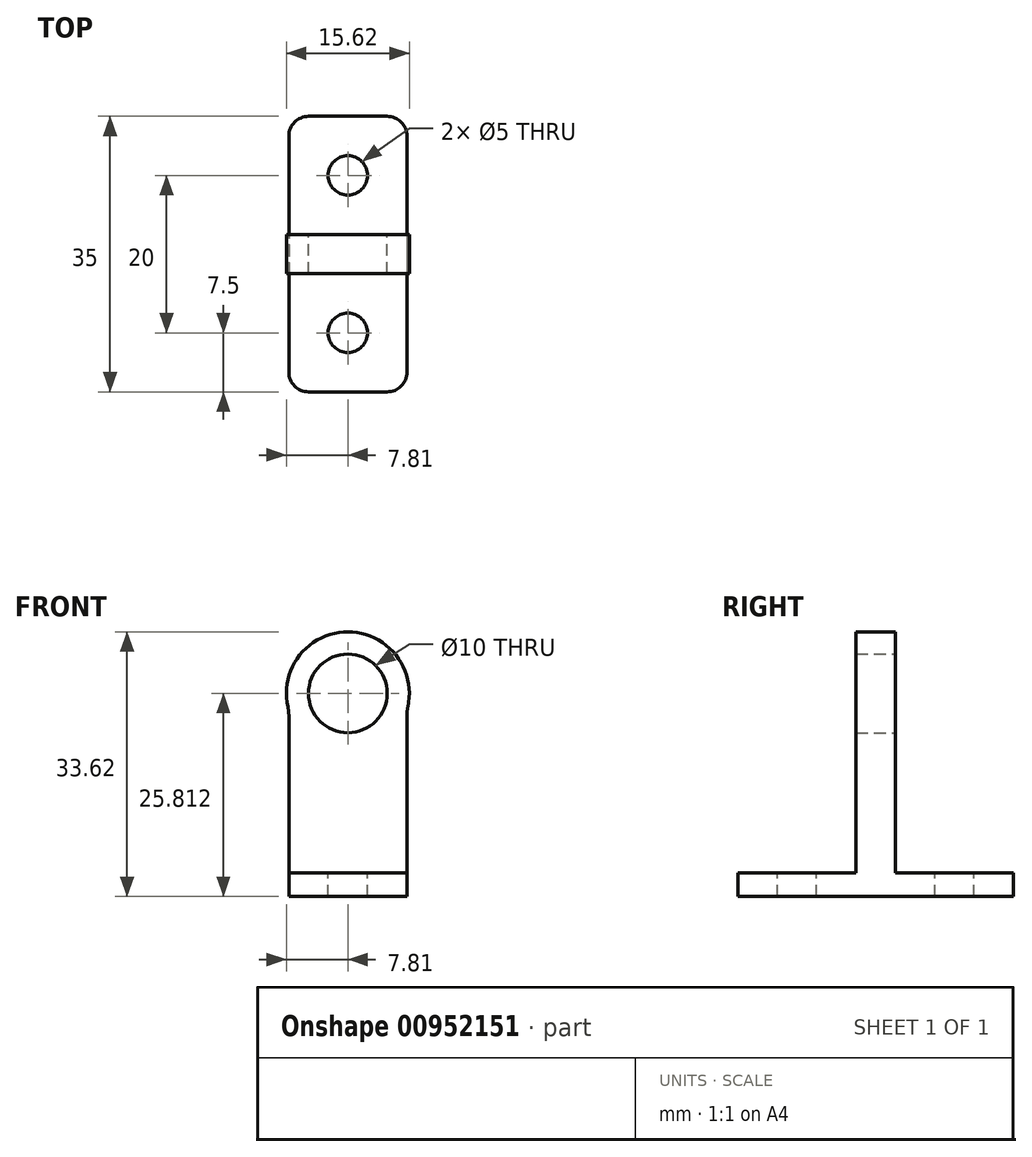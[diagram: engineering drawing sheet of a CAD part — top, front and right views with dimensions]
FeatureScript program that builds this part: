
annotation { "Feature Type Name" : "Feature", "Feature Type Description" : "" }
export const myFeature = defineFeature(function(context is Context, id is Id, definition is map)
    precondition{}
    {
        {
            var Q0;
            Q0=qCreatedBy(makeId("Top.planeOp"),FACE);
            var sketch = newSketch(context, id + "F0", { "sketchPlane" : qUnion([Q0])});
            skLineSegment(sketch, "E0.bottom", {"start": v(-7.5, 17.5) * mm, "end": v(7.5, 17.5) * mm});
            skLineSegment(sketch, "E0.top", {"start": v(-7.5, -17.5) * mm, "end": v(7.5, -17.5) * mm});
            skLineSegment(sketch, "E0.left", {"start": v(-7.5, 17.5) * mm, "end": v(-7.5, -17.5) * mm});
            skLineSegment(sketch, "E0.right", {"start": v(7.5, 17.5) * mm, "end": v(7.5, -17.5) * mm});
            skSolve(sketch);
        }
        {
            var Q0;
            Q0 = qSketchRegion(id + "F0", true);
            extrude(context, id + "F1", {"entities" : qUnion([Q0]), "depth" : 3 * mm, "offsetDistance" : 25 * mm});
        }
        {
            var Q0;
            Q0=makeQuery(id+"F1.opExtrude","SWEPT_EDGE",EDGE,{"disambiguationData":[OSD([sQuery(id+"F0.wireOp",EDGE,"E0.top"),sQuery(id+"F0.wireOp",EDGE,"E0.left")])]});
            var Q1;
            Q1=makeQuery(id+"F1.opExtrude","SWEPT_EDGE",EDGE,{"disambiguationData":[OSD([sQuery(id+"F0.wireOp",EDGE,"E0.top"),sQuery(id+"F0.wireOp",EDGE,"E0.right")])]});
            var Q2;
            Q2=makeQuery(id+"F1.opExtrude","SWEPT_EDGE",EDGE,{"disambiguationData":[OSD([sQuery(id+"F0.wireOp",EDGE,"E0.bottom"),sQuery(id+"F0.wireOp",EDGE,"E0.right")])]});
            var Q3;
            Q3=makeQuery(id+"F1.opExtrude","SWEPT_EDGE",EDGE,{"disambiguationData":[OSD([sQuery(id+"F0.wireOp",EDGE,"E0.bottom"),sQuery(id+"F0.wireOp",EDGE,"E0.left")])]});
            fillet(context, id + "F2", {"entities" : qUnion([Q0, Q1, Q2, Q3]), "radius" : 2.5 * mm, "tangentPropagation" : true, "allowEdgeOverflow" : false});
        }
        {
            var Q0;
            Q0=makeQuery(id+"F1.opExtrude","CAP_FACE",FACE,{"disambiguationData":[OSD([sQuery(id+"F0.wireOp",EDGE,"E0.bottom"),sQuery(id+"F0.wireOp",EDGE,"E0.top"),sQuery(id+"F0.wireOp",EDGE,"E0.left"),sQuery(id+"F0.wireOp",EDGE,"E0.right")])],"isStart":false});
            var sketch = newSketch(context, id + "F3", { "sketchPlane" : qUnion([Q0])});
            skLineSegment(sketch, "E1.bottom", {"start": v(-7.5, 2.5) * mm, "end": v(7.5, 2.5) * mm});
            skLineSegment(sketch, "E1.top", {"start": v(-7.5, -2.5) * mm, "end": v(7.5, -2.5) * mm});
            skLineSegment(sketch, "E1.left", {"start": v(-7.5, 2.5) * mm, "end": v(-7.5, -2.5) * mm});
            skLineSegment(sketch, "E1.right", {"start": v(7.5, 2.5) * mm, "end": v(7.5, -2.5) * mm});
            skSolve(sketch);
        }
        {
            var Q0;
            Q0 = qSketchRegion(id + "F3", true);
            extrude(context, id + "F4", {"entities" : qUnion([Q0]), "operationType" : NewBodyOperationType.ADD, "depth" : 25 * mm, "offsetDistance" : 25 * mm});
        }
        {
            var Q0;
            Q0=makeQuery(id+"F4.opExtrude","SWEPT_FACE",FACE,{"disambiguationData":[OSD([sQuery(id+"F3.wireOp",EDGE,"E1.bottom")])]});
            var sketch = newSketch(context, id + "F5", { "sketchPlane" : qUnion([Q0])});
            skCircle(sketch, "E2", {"center": v(0, 25.81) * mm, "radius": 7.81 * mm});
            skSolve(sketch);
        }
        {
            var Q0;
            Q0 = qSketchRegion(id + "F5", true);
            extrude(context, id + "F6", {"entities" : qUnion([Q0]), "operationType" : NewBodyOperationType.ADD, "depth" : 0 * mm, "offsetDistance" : 25 * mm, "hasSecondDirection" : true, "secondDirectionOppositeDirection" : true, "secondDirectionDepth" : 5 * mm});
        }
        {
            var Q0;
            Q0=makeQuery(id+"F6.boolean.opBoolean","MERGE",FACE,{"derivedFrom":[makeQuery(id+"F4.opExtrude","SWEPT_FACE",FACE,{"disambiguationData":[OSD([sQuery(id+"F3.wireOp",EDGE,"E1.bottom")])]}),makeQuery(id+"F6.opExtrude","CAP_FACE",FACE,{"disambiguationData":[OSD([sQuery(id+"F5.wireOp",EDGE,"E2")])],"isStart":false})]});
            var sketch = newSketch(context, id + "F7", { "sketchPlane" : qUnion([Q0])});
            skCircle(sketch, "E3", {"center": v(0, 25.81) * mm, "radius": 5 * mm});
            skSolve(sketch);
        }
        {
            var Q0;
            Q0 = qSketchRegion(id + "F7", true);
            extrude(context, id + "F8", {"entities" : qUnion([Q0]), "operationType" : NewBodyOperationType.REMOVE, "endBound" : BoundingType.THROUGH_ALL, "oppositeDirection" : true, "depth" : 25 * mm, "offsetDistance" : 25 * mm});
        }
        {
            var Q0;
            Q0=makeQuery(id+"F6.boolean.opBoolean","INTERSECT",EDGE,{"derivedFrom":[makeQuery(id+"F4.boolean.opBoolean","MERGE",FACE,{"derivedFrom":[makeQuery(id+"F1.opExtrude","SWEPT_FACE",FACE,{"disambiguationData":[OSD([sQuery(id+"F0.wireOp",EDGE,"E0.right")])]}),makeQuery(id+"F4.opExtrude","SWEPT_FACE",FACE,{"disambiguationData":[OSD([sQuery(id+"F3.wireOp",EDGE,"E1.right")])]})]}),makeQuery(id+"F6.opExtrude","SWEPT_FACE",FACE,{"disambiguationData":[OSD([sQuery(id+"F5.wireOp",EDGE,"E2")])]})]});
            var Q1;
            Q1=makeQuery(id+"F6.boolean.opBoolean","INTERSECT",EDGE,{"derivedFrom":[makeQuery(id+"F4.boolean.opBoolean","MERGE",FACE,{"derivedFrom":[makeQuery(id+"F1.opExtrude","SWEPT_FACE",FACE,{"disambiguationData":[OSD([sQuery(id+"F0.wireOp",EDGE,"E0.left")])]}),makeQuery(id+"F4.opExtrude","SWEPT_FACE",FACE,{"disambiguationData":[OSD([sQuery(id+"F3.wireOp",EDGE,"E1.left")])]})]}),makeQuery(id+"F6.opExtrude","SWEPT_FACE",FACE,{"disambiguationData":[OSD([sQuery(id+"F5.wireOp",EDGE,"E2")])]})]});
            fillet(context, id + "F9", {"entities" : qUnion([Q0, Q1]), "radius" : 5 * mm, "tangentPropagation" : true, "allowEdgeOverflow" : false});
        }
        {
            var Q0;
            {var subQ0=sQuery(id+"F0.wireOp",EDGE,"E0.left");var subQ1=sQuery(id+"F0.wireOp",EDGE,"E0.bottom");var subQ2=sQuery(id+"F0.wireOp",EDGE,"E0.right");Q0=makeQuery(id+"F4.boolean.opBoolean","SPLIT",FACE,{"disambiguationData":[TD([makeQuery(id+"F1.opExtrude","SWEPT_FACE",FACE,{"disambiguationData":[OSD([subQ1])]})])],"derivedFrom":makeQuery(id+"F1.opExtrude","CAP_FACE",FACE,{"disambiguationData":[OSD([subQ1,sQuery(id+"F0.wireOp",EDGE,"E0.top"),subQ0,subQ2])],"isStart":false})});}
            var sketch = newSketch(context, id + "F10", { "sketchPlane" : qUnion([Q0])});
            skCircle(sketch, "E4", {"center": v(0, 10) * mm, "radius": 2.5 * mm});
            skCircle(sketch, "E5", {"center": v(0, -10) * mm, "radius": 2.5 * mm});
            skSolve(sketch);
        }
        {
            var Q0;
            Q0 = qSketchRegion(id + "F10", true);
            extrude(context, id + "F11", {"entities" : qUnion([Q0]), "operationType" : NewBodyOperationType.REMOVE, "endBound" : BoundingType.THROUGH_ALL, "oppositeDirection" : true, "depth" : 25 * mm, "offsetDistance" : 25 * mm});
        }
    });
